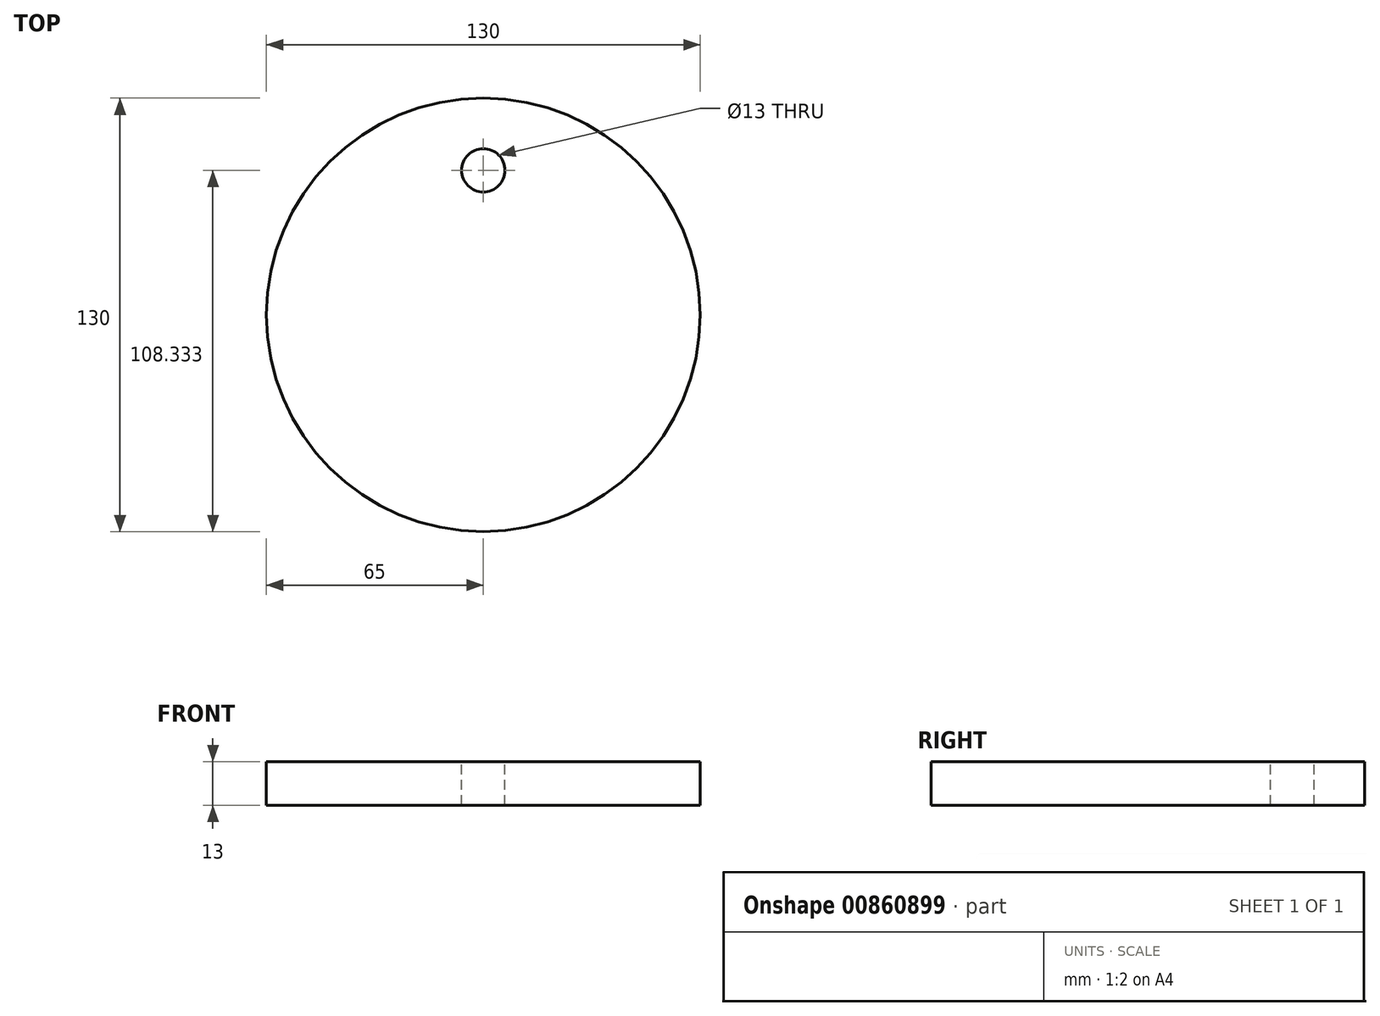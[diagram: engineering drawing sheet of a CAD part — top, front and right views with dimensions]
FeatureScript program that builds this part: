
annotation { "Feature Type Name" : "Feature", "Feature Type Description" : "" }
export const myFeature = defineFeature(function(context is Context, id is Id, definition is map)
    precondition{}
    {
        {
            assignVariable(context, id + "F0", {"name" : "BigCircle", "anyValue" : 130});
        }
        {
            assignVariable(context, id + "F1", {"name" : "Thickness", "anyValue" : getVariable(context, 'BigCircle') / 10});
        }
        {
            var Q0;
            Q0=qCreatedBy(makeId("Top.planeOp"),FACE);
            var sketch = newSketch(context, id + "F2", { "sketchPlane" : qUnion([Q0])});
            skCircle(sketch, "E0", {"center": v(0, 0) * mm, "radius": 65 * mm});
            skSolve(sketch);
        }
        {
            var Q0;
            Q0 = qSketchRegion(id + "F2", true);
            extrude(context, id + "F3", {"entities" : qUnion([Q0]), "depth" : (getVariable(context, 'Thickness')) * mm, "offsetDistance" : 25 * mm});
        }
        {
            var Q0;
            Q0=makeQuery(id+"F3.opExtrude","CAP_FACE",FACE,{"disambiguationData":[OSD([sQuery(id+"F2.wireOp",EDGE,"E0")])],"isStart":false});
            var sketch = newSketch(context, id + "F4", { "sketchPlane" : qUnion([Q0])});
            skCircle(sketch, "E1", {"center": v(0, 0) * mm, "radius": 43.33 * mm, "construction": true});
            skCircle(sketch, "E2", {"center": v(0, 43.33) * mm, "radius": 6.5 * mm});
            skSolve(sketch);
        }
        {
            var Q0;
            Q0=makeQuery(id+"F4.imprint","IMPRINT",FACE,{"disambiguationData":[TD([[makeQuery(id+"F4.imprint","IMPRINT",EDGE,{"derivedFrom":sQuery(id+"F4.wireOp",EDGE,"E2")}),1.0]])]});
            extrude(context, id + "F5", {"entities" : qUnion([Q0]), "operationType" : NewBodyOperationType.REMOVE, "endBound" : BoundingType.THROUGH_ALL, "oppositeDirection" : true, "depth" : 25 * mm, "offsetDistance" : 25 * mm});
        }
    });
